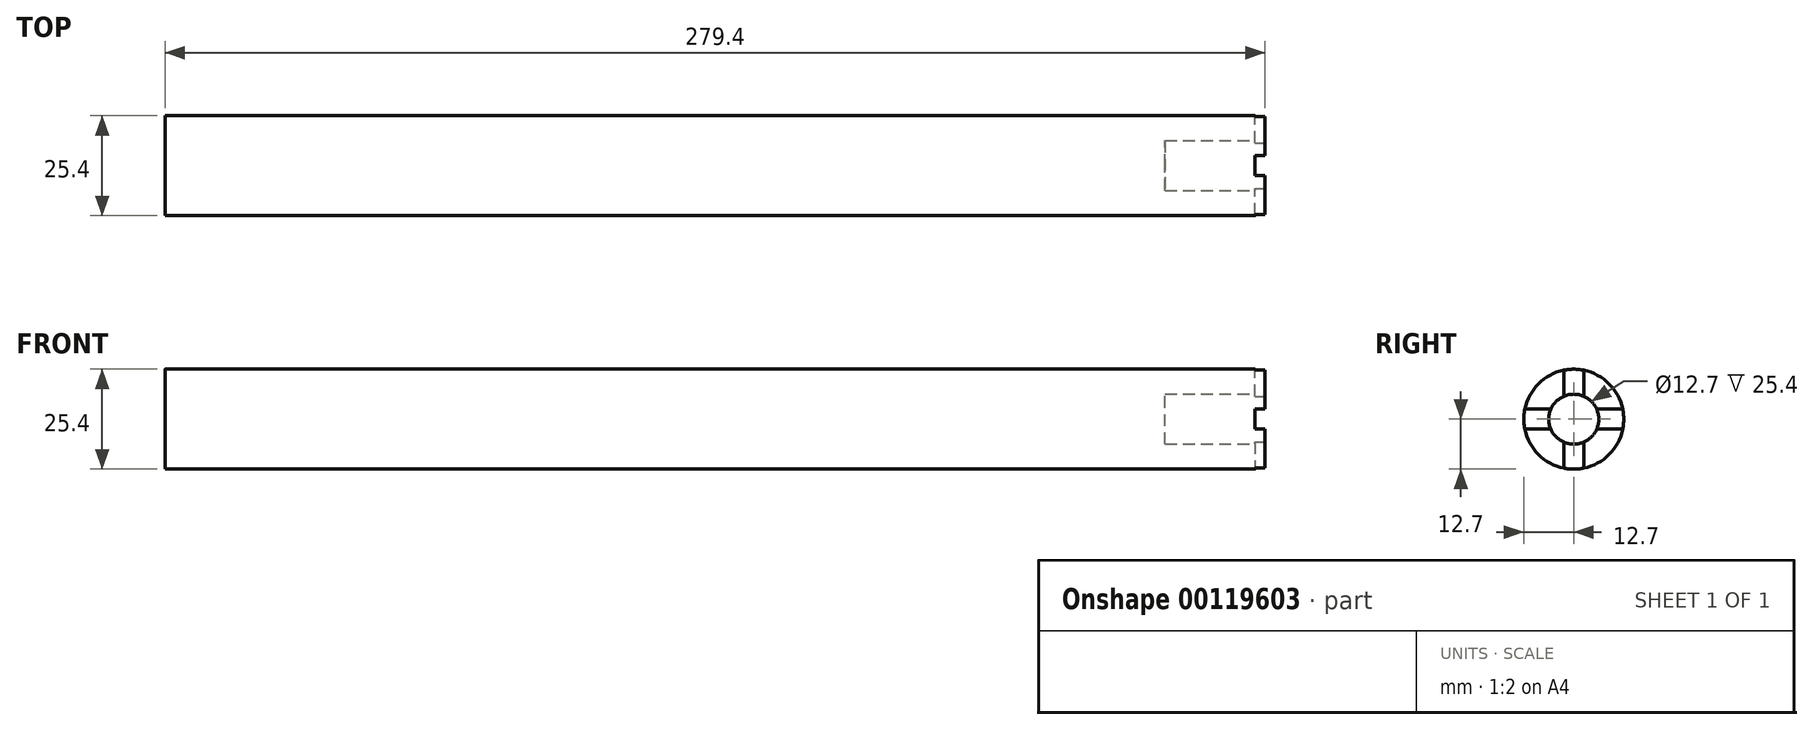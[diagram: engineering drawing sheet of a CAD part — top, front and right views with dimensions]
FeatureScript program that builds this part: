
annotation { "Feature Type Name" : "Feature", "Feature Type Description" : "" }
export const myFeature = defineFeature(function(context is Context, id is Id, definition is map)
    precondition{}
    {
        {
            var Q0;
            Q0=qCreatedBy(makeId("Right.planeOp"),FACE);
            var sketch = newSketch(context, id + "F0", { "sketchPlane" : qUnion([Q0])});
            skCircle(sketch, "E0", {"center": v(0, 0) * mm, "radius": 12.7 * mm});
            skSolve(sketch);
        }
        {
            var Q0;
            Q0 = qSketchRegion(id + "F0", true);
            extrude(context, id + "F1", {"entities" : qUnion([Q0]), "depth" : 279.4 * mm});
        }
        {
            var Q0;
            Q0=makeQuery(id+"F1.opExtrude","CAP_FACE",FACE,{"disambiguationData":[OSD([sQuery(id+"F0.wireOp",EDGE,"E0")])],"isStart":false});
            var sketch = newSketch(context, id + "F2", { "sketchPlane" : qUnion([Q0])});
            skCircle(sketch, "E1", {"center": v(0, 0) * mm, "radius": 6.35 * mm});
            skSolve(sketch);
        }
        {
            var Q0;
            Q0 = qSketchRegion(id + "F2", true);
            extrude(context, id + "F3", {"entities" : qUnion([Q0]), "operationType" : NewBodyOperationType.REMOVE, "oppositeDirection" : true, "depth" : 25.4 * mm});
        }
        {
            var Q0;
            Q0=makeQuery(id+"F1.opExtrude","CAP_FACE",FACE,{"disambiguationData":[OSD([sQuery(id+"F0.wireOp",EDGE,"E0")])],"isStart":false});
            var sketch = newSketch(context, id + "F4", { "sketchPlane" : qUnion([Q0])});
            skLineSegment(sketch, "E2", {"start": v(-12.7, 0) * mm, "end": v(12.7, 0) * mm, "construction": true});
            skLineSegment(sketch, "E3", {"start": v(0, 12.7) * mm, "end": v(0, -12.7) * mm, "construction": true});
            skPoint(sketch, "E3.startSnap0", {"position": v(0, 0) * mm});
            skLineSegment(sketch, "E4", {"start": v(-12.44, -2.54) * mm, "end": v(-5.82, -2.54) * mm});
            skLineSegment(sketch, "E5", {"start": v(-12.44, 2.54) * mm, "end": v(-5.82, 2.54) * mm});
            skLineSegment(sketch, "E6", {"start": v(-2.54, 12.44) * mm, "end": v(-2.54, 5.82) * mm});
            skLineSegment(sketch, "E7", {"start": v(2.54, 12.44) * mm, "end": v(2.54, 5.82) * mm});
            skLineSegment(sketch, "E8", {"start": v(5.82, 2.54) * mm, "end": v(12.44, 2.54) * mm});
            skLineSegment(sketch, "E9", {"start": v(5.82, -2.54) * mm, "end": v(12.44, -2.54) * mm});
            skLineSegment(sketch, "E10", {"start": v(2.54, -5.82) * mm, "end": v(2.54, -12.44) * mm});
            skLineSegment(sketch, "E11", {"start": v(-2.54, -5.82) * mm, "end": v(-2.54, -12.44) * mm});
            skLineSegment(sketch, "E12", {"start": v(-2.54, 5.82) * mm, "end": v(2.54, 5.82) * mm});
            skLineSegment(sketch, "E13", {"start": v(5.82, 2.54) * mm, "end": v(5.82, -2.54) * mm});
            skLineSegment(sketch, "E14", {"start": v(2.54, -5.82) * mm, "end": v(-2.54, -5.82) * mm});
            skLineSegment(sketch, "E15", {"start": v(-5.82, -2.54) * mm, "end": v(-5.82, 2.54) * mm});
            skLineSegment(sketch, "E16", {"start": v(-2.54, 12.44) * mm, "end": v(-2.54, 13.38) * mm});
            skLineSegment(sketch, "E17", {"start": v(-2.54, 13.38) * mm, "end": v(2.54, 13.38) * mm});
            skLineSegment(sketch, "E18", {"start": v(2.54, 13.38) * mm, "end": v(2.54, 12.44) * mm});
            skLineSegment(sketch, "E19", {"start": v(12.44, 2.54) * mm, "end": v(13.55, 2.54) * mm});
            skLineSegment(sketch, "E20", {"start": v(13.55, 2.54) * mm, "end": v(13.55, -2.54) * mm});
            skLineSegment(sketch, "E21", {"start": v(13.55, -2.54) * mm, "end": v(12.44, -2.54) * mm});
            skLineSegment(sketch, "E22", {"start": v(2.54, -12.44) * mm, "end": v(2.54, -13.7) * mm});
            skLineSegment(sketch, "E23", {"start": v(2.54, -13.7) * mm, "end": v(-2.54, -13.7) * mm});
            skLineSegment(sketch, "E24", {"start": v(-2.54, -13.7) * mm, "end": v(-2.54, -12.44) * mm});
            skLineSegment(sketch, "E25", {"start": v(-12.44, -2.54) * mm, "end": v(-13.53, -2.54) * mm});
            skLineSegment(sketch, "E26", {"start": v(-13.53, -2.54) * mm, "end": v(-13.53, 2.54) * mm});
            skLineSegment(sketch, "E27", {"start": v(-13.53, 2.54) * mm, "end": v(-12.44, 2.54) * mm});
            skSolve(sketch);
        }
        {
            var Q0;
            Q0 = qSketchRegion(id + "F4", true);
            extrude(context, id + "F5", {"entities" : qUnion([Q0]), "operationType" : NewBodyOperationType.REMOVE, "oppositeDirection" : true, "depth" : 2.54 * mm});
        }
    });
